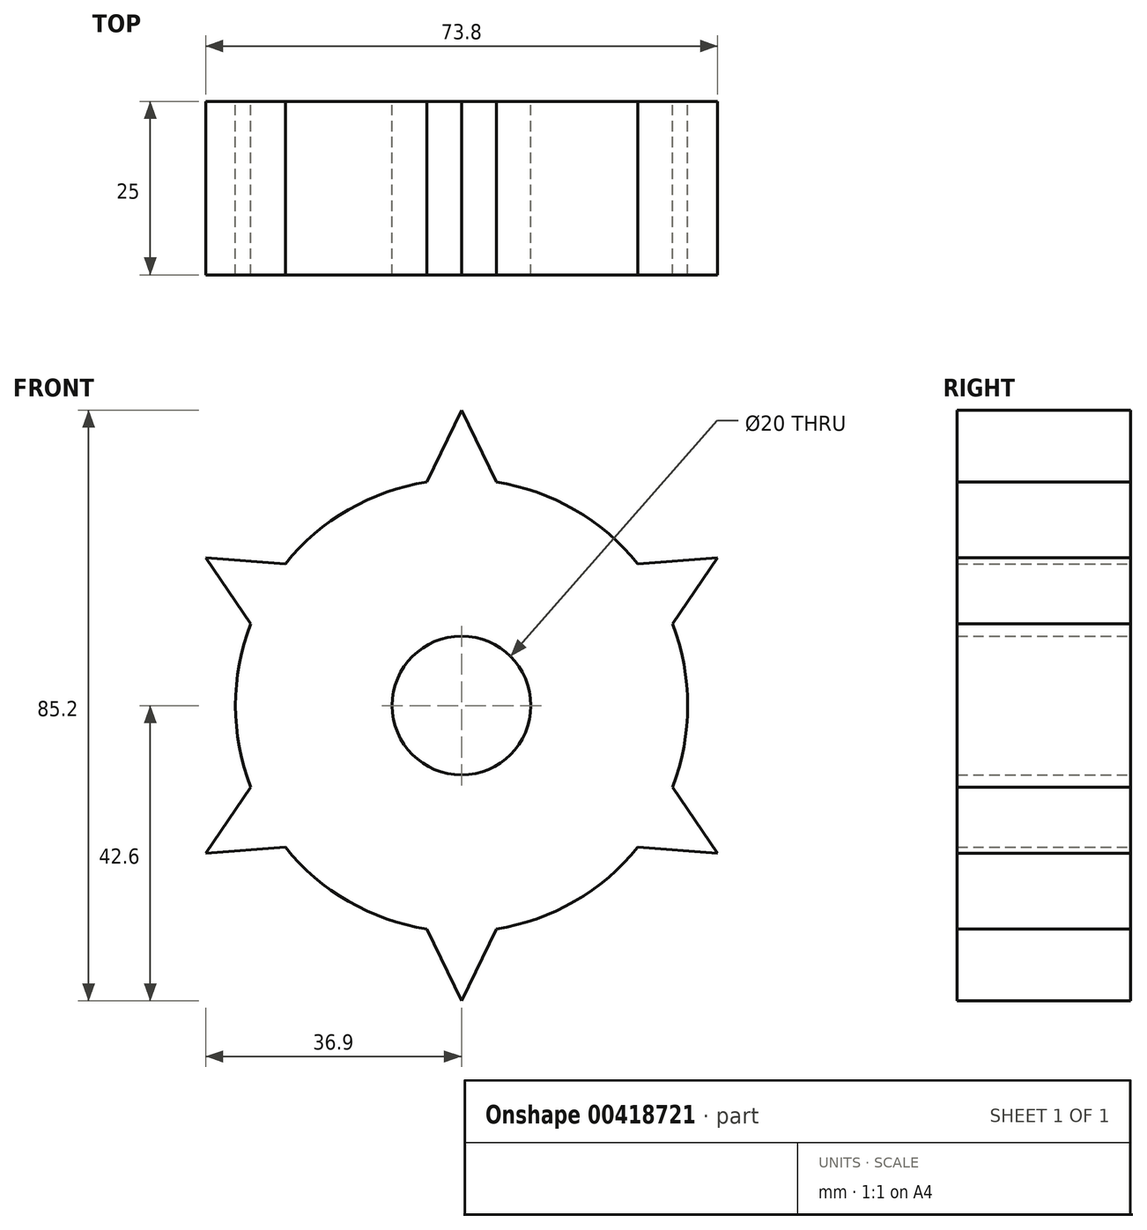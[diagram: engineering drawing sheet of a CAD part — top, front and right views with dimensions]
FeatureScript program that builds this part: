
annotation { "Feature Type Name" : "Feature", "Feature Type Description" : "" }
export const myFeature = defineFeature(function(context is Context, id is Id, definition is map)
    precondition{}
    {
        {
            var Q0;
            Q0=qCreatedBy(makeId("Front.planeOp"),FACE);
            var sketch = newSketch(context, id + "F0", { "sketchPlane" : qUnion([Q0])});
            skCircle(sketch, "E0", {"center": v(0, 0) * mm, "radius": 32.6 * mm});
            skPoint(sketch, "E1", {"position": v(0, 32.6) * mm});
            skLineSegment(sketch, "E2", {"start": v(0, 32.6) * mm, "end": v(0, 48.8) * mm, "construction": true});
            skLineSegment(sketch, "E3", {"start": v(0, 42.6) * mm, "end": v(-5, 32.22) * mm});
            skLineSegment(sketch, "E4.MirrorCS", {"start": v(0, 42.6) * mm, "end": v(5, 32.22) * mm});
            skLineSegment(sketch, "E5.1.0", {"start": v(-36.9, 21.3) * mm, "end": v(-25.4, 20.44) * mm});
            skLineSegment(sketch, "E5.1.1", {"start": v(-36.9, 21.3) * mm, "end": v(-30.4, 11.78) * mm});
            skLineSegment(sketch, "E5.2.0", {"start": v(-36.9, -21.3) * mm, "end": v(-30.4, -11.78) * mm});
            skLineSegment(sketch, "E5.2.1", {"start": v(-36.9, -21.3) * mm, "end": v(-25.4, -20.44) * mm});
            skLineSegment(sketch, "E5.3.0", {"start": v(0, -42.6) * mm, "end": v(-5, -32.22) * mm});
            skLineSegment(sketch, "E5.3.1", {"start": v(0, -42.6) * mm, "end": v(5, -32.22) * mm});
            skLineSegment(sketch, "E5.4.0", {"start": v(36.9, -21.3) * mm, "end": v(25.4, -20.44) * mm});
            skLineSegment(sketch, "E5.4.1", {"start": v(36.9, -21.3) * mm, "end": v(30.4, -11.78) * mm});
            skLineSegment(sketch, "E5.5.0", {"start": v(36.9, 21.3) * mm, "end": v(30.4, 11.78) * mm});
            skLineSegment(sketch, "E5.5.1", {"start": v(36.9, 21.3) * mm, "end": v(25.4, 20.44) * mm});
            skSolve(sketch);
        }
        {
            var Q0;
            Q0 = qSketchRegion(id + "F0", true);
            extrude(context, id + "F1", {"entities" : qUnion([Q0]), "depth" : 25 * mm});
        }
        {
            var Q0;
            {var subQ0=sQuery(id+"F0.wireOp",EDGE,"E0");var subQ8=makeQuery(id+"F0.imprint","INTERSECT",VERTEX,{"derivedFrom":[subQ0,sQuery(id+"F0.wireOp",EDGE,"E5.3.0")]});Q0=makeQuery(id+"F0.imprint","IMPRINT",FACE,{"disambiguationData":[TD([[makeQuery(id+"F0.imprint","IMPRINT",EDGE,{"disambiguationData":[TD([[subQ8,-1.0]])],"derivedFrom":subQ0}),1.0]])]});}
            var sketch = newSketch(context, id + "F2", { "sketchPlane" : qUnion([Q0])});
            skCircle(sketch, "E6", {"center": v(0, 0) * mm, "radius": 10 * mm});
            skSolve(sketch);
        }
        {
            var Q0;
            Q0 = qSketchRegion(id + "F2", true);
            extrude(context, id + "F3", {"entities" : qUnion([Q0]), "operationType" : NewBodyOperationType.REMOVE, "depth" : 31 * mm});
        }
    });
